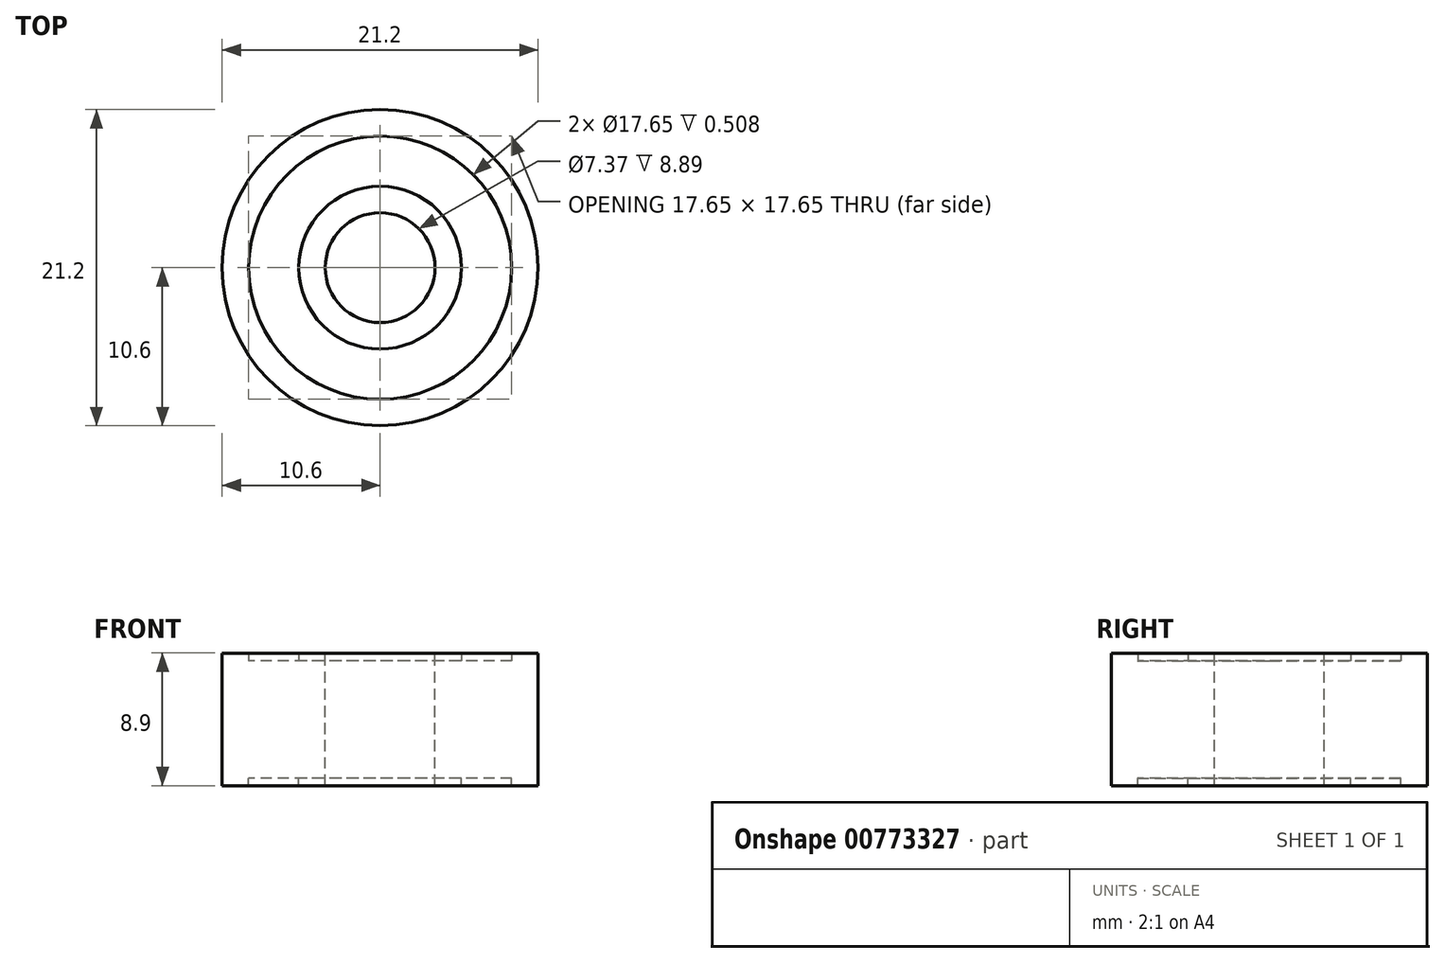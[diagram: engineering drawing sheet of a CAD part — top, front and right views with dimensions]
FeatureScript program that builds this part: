
annotation { "Feature Type Name" : "Feature", "Feature Type Description" : "" }
export const myFeature = defineFeature(function(context is Context, id is Id, definition is map)
    precondition{}
    {
        {
            var Q0;
            Q0=qCreatedBy(makeId("Top.planeOp"),FACE);
            var sketch = newSketch(context, id + "F0", { "sketchPlane" : qUnion([Q0])});
            skCircle(sketch, "E0", {"center": v(0, 0) * mm, "radius": 10.6 * mm});
            skSolve(sketch);
        }
        {
            var Q0;
            Q0 = qSketchRegion(id + "F0", true);
            extrude(context, id + "F1", {"entities" : qUnion([Q0]), "depth" : 4.44 * mm, "offsetDistance" : 25.4 * mm});
        }
        {
            var Q0;
            Q0=makeQuery(id+"F1.opExtrude","CAP_FACE",FACE,{"disambiguationData":[OSD([sQuery(id+"F0.wireOp",EDGE,"E0")])],"isStart":false});
            shell(context, id + "F2", {"entities" : qUnion([Q0]), "thickness" : 1.78 * mm});
        }
        {
            var Q0;
            Q0=qCreatedBy(makeId("Top.planeOp"),FACE);
            var sketch = newSketch(context, id + "F3", { "sketchPlane" : qUnion([Q0])});
            skCircle(sketch, "E1", {"center": v(0, 0) * mm, "radius": 8.83 * mm});
            skSolve(sketch);
        }
        {
            var Q0;
            Q0 = qSketchRegion(id + "F3", true);
            extrude(context, id + "F4", {"entities" : qUnion([Q0]), "operationType" : NewBodyOperationType.ADD, "depth" : 3.94 * mm, "offsetDistance" : 25.4 * mm});
        }
        {
            var Q0;
            Q0=makeQuery(id+"F4.opExtrude","CAP_FACE",FACE,{"disambiguationData":[OSD([sQuery(id+"F3.wireOp",EDGE,"E1")])],"isStart":false});
            var sketch = newSketch(context, id + "F5", { "sketchPlane" : qUnion([Q0])});
            skCircle(sketch, "E2", {"center": v(0, 0) * mm, "radius": 5.46 * mm});
            skSolve(sketch);
        }
        {
            var Q0;
            Q0 = qSketchRegion(id + "F5", true);
            extrude(context, id + "F6", {"entities" : qUnion([Q0]), "operationType" : NewBodyOperationType.ADD, "depth" : 0.5 * mm, "offsetDistance" : 25.4 * mm});
        }
        {
            var Q0;
            Q0=makeQuery(id+"F6.opExtrude","CAP_FACE",FACE,{"disambiguationData":[OSD([sQuery(id+"F5.wireOp",EDGE,"E2")])],"isStart":false});
            var sketch = newSketch(context, id + "F7", { "sketchPlane" : qUnion([Q0])});
            skCircle(sketch, "E3", {"center": v(0, 0) * mm, "radius": 3.68 * mm});
            skSolve(sketch);
        }
        {
            var Q0;
            Q0=makeQuery(id+"F7.imprint","IMPRINT",FACE,{"disambiguationData":[TD([[makeQuery(id+"F7.imprint","IMPRINT",EDGE,{"derivedFrom":sQuery(id+"F7.wireOp",EDGE,"E3")}),1.0]])]});
            extrude(context, id + "F8", {"entities" : qUnion([Q0]), "operationType" : NewBodyOperationType.REMOVE, "oppositeDirection" : true, "depth" : 25.4 * mm, "offsetDistance" : 25.4 * mm});
        }
        {
            var Q0;
            Q0=makeQuery(id+"F1.opExtrude","SWEPT_BODY",BODY,{"disambiguationData":[OSD([sQuery(id+"F0.wireOp",EDGE,"E0")])]});
            var Q1;
            Q1=qCreatedBy(makeId("Top.planeOp"),FACE);
            mirror(context, id + "F9", {"operationType" : NewBodyOperationType.ADD, "entities" : qUnion([Q0]), "mirrorPlane" : qUnion([Q1])});
        }
    });
